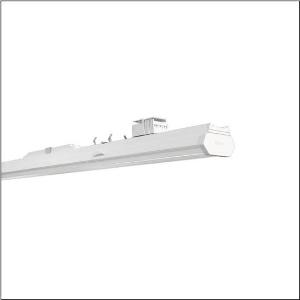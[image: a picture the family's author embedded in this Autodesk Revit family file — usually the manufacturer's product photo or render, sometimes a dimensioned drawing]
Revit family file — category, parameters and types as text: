
# Revit family: licross_11_protected_ho_51tp12dn4fxm3c
name_source: partatom
category: Lighting Fixtures
units: mm (PartAtom-declared; Revit-internal decimal feet)

## family parameters
Cut with Voids When Loaded = No
Host = Face
Light Source = No
Part Type = Normal
Room Calculation Point = No
Round Connector Dimension = Use Diameter
Shared = No

## types (1)
- --- (1 x LED, 970 lm, 7.4 W, 4000K)
    Apparent Load = 7 VA
    CIE Flux Codes = 70 91 97 98 100
    Color Rendering = 80
    Color Temperature = 4000K
    Default Elevation = 1800 mm
    Description = Licross 11 Protected HO, luminaire insert, of sheet steel, galvanised, coil coated, white, length: 1.500mm, width: 90mm, height: 101mm, LED rated luminous flux: 15.270lm, light colour: 840, SDCM (Standard Deviation of Colour Matching)MacAdam ≤ 2 SDCM (initial), control gear: DALI 2 (for two DALI lines), with plug, 6-pole, with phase selection, for trunking rail, 14-core, mains connection: 220..240V, AC, 50/60Hz, rated input power: 91W, for trunking rail, 14-core, internal wiring halogen-free, for emergency light function, converter,control gear: single battery element, battery: LiFePO4, 9Ah, primary light control with lens, of plastic, primary optical cover: cover, of PMMA, light emission: direct distribution, primary light characteristic: symmetric, protection rating (complete): IP64, insulation class (complete): insulation class I (protective earthing), certification: CE, UKCA, protection symbol: D if used in an environment with conductive dust loads with corresponding accessories, impact resistance: IK06, permissible ambient temperature for indoor applications: +5..+30°C, standard: EN 60598-2-22, LABS conformity tested according to VDMA 24364:2018-05, reducing of maximum allowable ambient temperature of 5°C with ceiling mounting, corresponds to IFS (International Featured Standards) requirements for safety and quality in the food industry, The light source and the operating device comply with the requirements of the Ecodesign Regulation (EU) 2019/2020 and are replaceable in accordance with this regulation, packaging unit: 1 piece
    Height = 92 mm
    Lamp = 1 x LED
    Lamp Light Flux = 970 lm
    Lamp Power = 7.4 W
    Lamp count = 1
    Length = 1500 mm
    Luminous efficacy = 131 lm/W
    Manufacturer = Siteco
    ModVariant = No
    Model = 51TP12DN4FXM3C
    Mounting Place = Ceiling
    Mounting Type = Pendant
    Number of Poles = 1
    OnlyDefault = Yes
    Power Factor = 1
    Product Name = Licross 11 Protected HO
    Product group = luminaire insert | ceiling pendant
    ProductGroupID = 901
    Protection Class = Protection class I
    Protection Degree = IP 64
    RLX_Detail_Level = 1
    RLX_Emergency_Light_Flux = 0 lm
    RLX_Emergency_Type = 0
    RLX_Emergency_Type_DB = No
    RlxData = <blob elided: 25125 chars, md5=72cebbe8>
    Socket = socket
    Standby Power = 0 W
    System Light Flux = 970 lm
    System Power = 7 W
    Type Comments = : emergency light operation: 3 h
    Type Image = l_1256148.jpg
    URL = http://relux.com
    VarID = @adj_096343
    Voltage = 0 V
    Weight = 0.00 kg
    Width = 88 mm

## geometry (parser evidence)
native form markers: Blend x4, Sweep x9
no freeform markers — native parametric forms only
